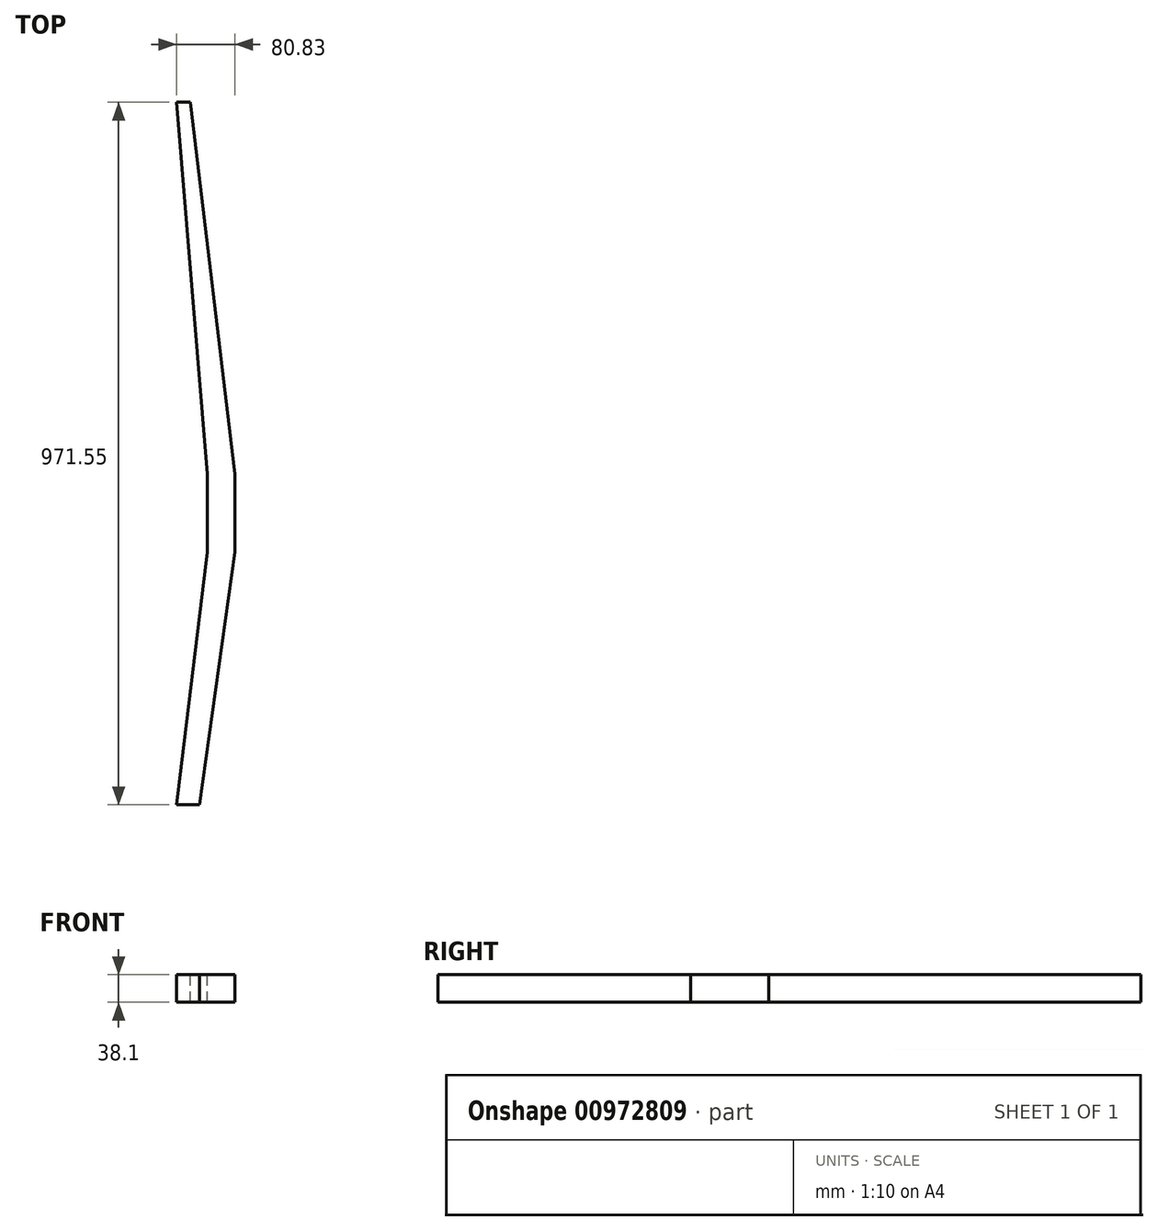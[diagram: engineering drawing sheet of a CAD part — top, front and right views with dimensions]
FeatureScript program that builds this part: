
annotation { "Feature Type Name" : "Feature", "Feature Type Description" : "" }
export const myFeature = defineFeature(function(context is Context, id is Id, definition is map)
    precondition{}
    {
        {
            var Q0;
            Q0=qCreatedBy(makeId("Front.planeOp"),FACE);
            var sketch = newSketch(context, id + "F0", { "sketchPlane" : qUnion([Q0])});
            skLineSegment(sketch, "E0.bottom", {"start": v(0, 0) * mm, "end": v(88.9, 0) * mm});
            skLineSegment(sketch, "E0.top", {"start": v(0, 38.1) * mm, "end": v(88.9, 38.1) * mm});
            skLineSegment(sketch, "E0.left", {"start": v(0, 0) * mm, "end": v(0, 38.1) * mm});
            skLineSegment(sketch, "E0.right", {"start": v(88.9, 0) * mm, "end": v(88.9, 38.1) * mm});
            skSolve(sketch);
        }
        {
            var Q0;
            Q0=makeQuery(id+"F0.imprint","IMPRINT",FACE,{"disambiguationData":[TD([[makeQuery(id+"F0.imprint","IMPRINT",EDGE,{"derivedFrom":sQuery(id+"F0.wireOp",EDGE,"E0.bottom")}),1.0]])]});
            extrude(context, id + "F1", {"entities" : qUnion([Q0]), "oppositeDirection" : true, "depth" : 971.55 * mm, "offsetDistance" : 25.4 * mm});
        }
        {
            var Q0;
            Q0=makeQuery(id+"F1.opExtrude","SWEPT_FACE",FACE,{"disambiguationData":[OSD([sQuery(id+"F0.wireOp",EDGE,"E0.top")])]});
            var sketch = newSketch(context, id + "F2", { "sketchPlane" : qUnion([Q0])});
            skLineSegment(sketch, "E1", {"start": v(80.83, 349.25) * mm, "end": v(80.83, 457.2) * mm});
            skLineSegment(sketch, "E2", {"start": v(80.83, 457.2) * mm, "end": v(19.05, 971.55) * mm});
            skLineSegment(sketch, "E3", {"start": v(19.05, 971.55) * mm, "end": v(0, 971.55) * mm});
            skLineSegment(sketch, "E4", {"start": v(0, 971.55) * mm, "end": v(42.73, 457.2) * mm});
            skLineSegment(sketch, "E5", {"start": v(42.73, 457.2) * mm, "end": v(42.73, 349.25) * mm});
            skLineSegment(sketch, "E6", {"start": v(42.73, 349.25) * mm, "end": v(0, 0) * mm});
            skLineSegment(sketch, "E7", {"start": v(0, 0) * mm, "end": v(31.75, 0) * mm});
            skLineSegment(sketch, "E8", {"start": v(31.75, 0) * mm, "end": v(80.83, 349.25) * mm});
            skSolve(sketch);
        }
        {
            var Q0;
            Q0=makeQuery(id+"F2.imprint","IMPRINT",FACE,{"disambiguationData":[TD([[makeQuery(id+"F2.imprint","IMPRINT",EDGE,{"derivedFrom":sQuery(id+"F2.wireOp",EDGE,"E4")}),-1.0]])]});
            var Q1;
            Q1=makeQuery(id+"F2.imprint","IMPRINT",FACE,{"disambiguationData":[TD([[makeQuery(id+"F2.imprint","IMPRINT",EDGE,{"derivedFrom":sQuery(id+"F2.wireOp",EDGE,"E1")}),-1.0]])]});
            extrude(context, id + "F3", {"entities" : qUnion([Q0, Q1]), "operationType" : NewBodyOperationType.REMOVE, "endBound" : BoundingType.THROUGH_ALL, "oppositeDirection" : true, "depth" : 25.4 * mm, "offsetDistance" : 25.4 * mm});
        }
    });
